# Revit family: Дверь ДПО-230
name_source: partatom
category: Двери
revit_build: Autodesk Revit 2017 (Build: 20160225_1515(x64)
units: mm (PartAtom-declared; Revit-internal decimal feet)

## family parameters
Всегда вертикально = Да
Заголовок OmniClass = Doors
Номер OmniClass = 23.30.10.00
Общий = Нет
Основа = Стена
При загрузке вырезать с полостями = Нет
Точка расчета площади = Нет

## types (14) — shared parameters
Выступ каркаса внут. = 25 мм
Выступ каркаса нар. = 25 мм
Группа модели = ДПО-Огнедекор
Замыкание стены = По основе
Изготовитель = ДВР Центр, г.Москва
Материал_коробки = Сталь, белый
Материал_створки = Сталь, белый
Минимальная высота = 1200 мм
Минимальная ширина = 800 мм
Огнестойкость = EIW-30
Описание = Дверь противопожарная остекленная
Толщина = 50 мм
Функция = Внутренние слои
Ширина каркаса = 75 мм

## per-type parameters (varying)
| type | Высота | Левая | Правая | Ширина | Ширина С1 | Ширина С2 | Ширина левой створки | Ширина правой створки | Ширина створки равнопольной двери |
| ДПО-Огнедекор-02/30 21-13 (8) ПТ | 2070 мм | Нет | Да | 1270 мм | 856 мм | 409 мм | 353 мм | 800 мм | 577 мм |
| ДПО-Огнедекор-02/30 21-15 ПТ | 2070 мм | Нет | Да | 1470 мм | 733 мм | 733 мм | 677 мм | 677 мм | 677 мм |
| ДПО-Огнедекор-02/30 24-13 (9) ПТ | 2370 мм | Нет | Да | 1270 мм | 956 мм | 309 мм | 253 мм | 900 мм | 577 мм |
| ДПО-Огнедекор-02/30 24-13 (8) ПТ | 2370 мм | Нет | Да | 1270 мм | 856 мм | 409 мм | 353 мм | 800 мм | 577 мм |
| ДПО-Огнедекор-02/30 21-13 (9) ПТ | 2070 мм | Нет | Да | 1270 мм | 956 мм | 309 мм | 253 мм | 900 мм | 577 мм |
| ДПО-Огнедекор-02/30 21-13 (9) ЛТ | 2070 мм | Да | Нет | 1270 мм | 307 мм | 958 мм | 902 мм | 251 мм | 577 мм |
| ДПО-Огнедекор-02/30 21-13 (8) ЛТ | 2070 мм | Да | Нет | 1270 мм | 409 мм | 856 мм | 800 мм | 353 мм | 577 мм |
| ДПО-Огнедекор-02/30 21-15 ЛТ | 2070 мм | Да | Нет | 1470 мм | 733 мм | 733 мм | 677 мм | 677 мм | 677 мм |
| ДПО-Огнедекор-02/30 24-13 (9) ЛТ | 2370 мм | Да | Нет | 1270 мм | 309 мм | 956 мм | 900 мм | 253 мм | 577 мм |
| ДПО-Огнедекор-02/30 24-13 (8) ЛТ | 2370 мм | Да | Нет | 1270 мм | 409 мм | 856 мм | 800 мм | 353 мм | 577 мм |
| ДПО-Огнедекор-02/30 24-15 ПТ | 2370 мм | Нет | Да | 1470 мм | 733 мм | 733 мм | 677 мм | 677 мм | 677 мм |
| ДПО-Огнедекор-02/30 24-15 ЛТ | 2370 мм | Да | Нет | 1470 мм | 733 мм | 733 мм | 677 мм | 677 мм | 677 мм |
| ДПО-Огнедекор-02/30 21-18 ПТ | 2070 мм | Нет | Да | 1770 мм | 883 мм | 883 мм | 827 мм | 827 мм | 827 мм |
| ДПО-Огнедекор-02/30 21-18 ЛТ | 2070 мм | Да | Нет | 1770 мм | 883 мм | 883 мм | 827 мм | 827 мм | 827 мм |
